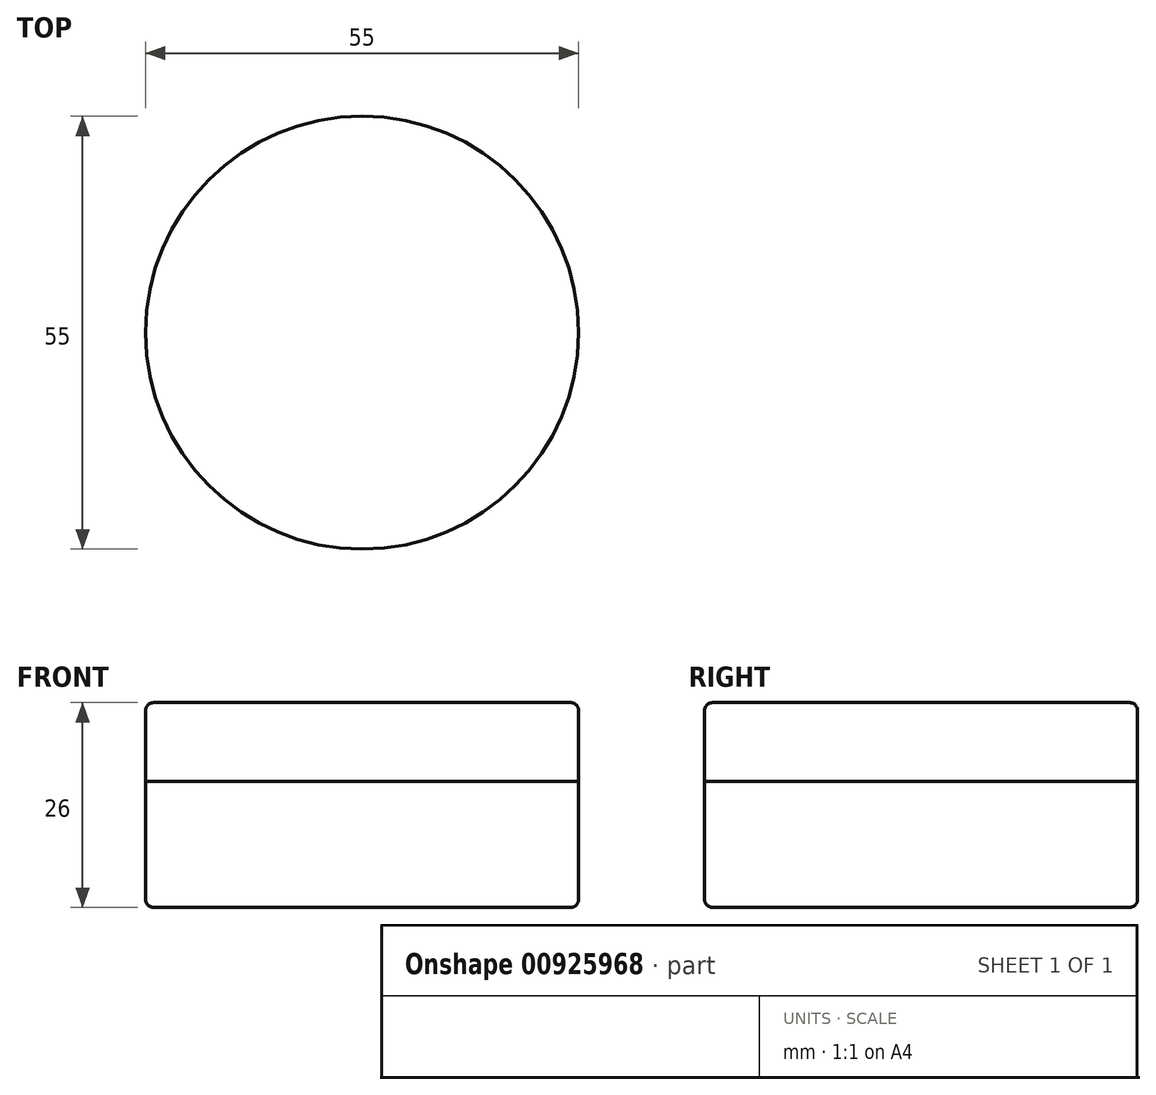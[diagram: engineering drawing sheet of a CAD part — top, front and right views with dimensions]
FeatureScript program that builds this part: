
annotation { "Feature Type Name" : "Feature", "Feature Type Description" : "" }
export const myFeature = defineFeature(function(context is Context, id is Id, definition is map)
    precondition{}
    {
        {
            var Q0;
            Q0=qCreatedBy(makeId("Top.planeOp"),FACE);
            var sketch = newSketch(context, id + "F0", { "sketchPlane" : qUnion([Q0])});
            skCircle(sketch, "E0", {"center": v(0, 0) * mm, "radius": 27.5 * mm});
            skSolve(sketch);
        }
        {
            var Q0;
            Q0=qSketchRegion(id+"F0",true);
            extrude(context, id + "F1", {"entities" : qUnion([Q0]), "depth" : 16 * mm, "offsetDistance" : 25 * mm});
        }
        {
            var Q0;
            Q0=makeQuery(id+"F1.opExtrude","CAP_FACE",FACE,{"disambiguationData":[OSD([sQuery(id+"F0.wireOp",EDGE,"E0")])],"isStart":false});
            var sketch = newSketch(context, id + "F2", { "sketchPlane" : qUnion([Q0])});
            skCircle(sketch, "E1.0", {"center": v(0, 0) * mm, "radius": 27.5 * mm});
            skSolve(sketch);
        }
        {
            var Q0;
            Q0=qSketchRegion(id+"F2",true);
            extrude(context, id + "F3", {"entities" : qUnion([Q0]), "depth" : 10 * mm, "offsetDistance" : 25 * mm});
        }
        {
            var Q0;
            Q0=makeQuery(id+"F3.opExtrude","CAP_EDGE",EDGE,{"disambiguationData":[OSD([sQuery(id+"F2.wireOp",EDGE,"E1.0")])],"isStart":false});
            fillet(context, id + "F4", {"entities" : qUnion([Q0]), "radius" : 1 * mm, "tangentPropagation" : true, "allowEdgeOverflow" : false});
        }
        {
            var Q0;
            Q0=makeQuery(id+"F1.opExtrude","CAP_EDGE",EDGE,{"disambiguationData":[OSD([sQuery(id+"F0.wireOp",EDGE,"E0")])],"isStart":true});
            fillet(context, id + "F5", {"entities" : qUnion([Q0]), "radius" : 1 * mm, "tangentPropagation" : true, "allowEdgeOverflow" : false});
        }
    });
